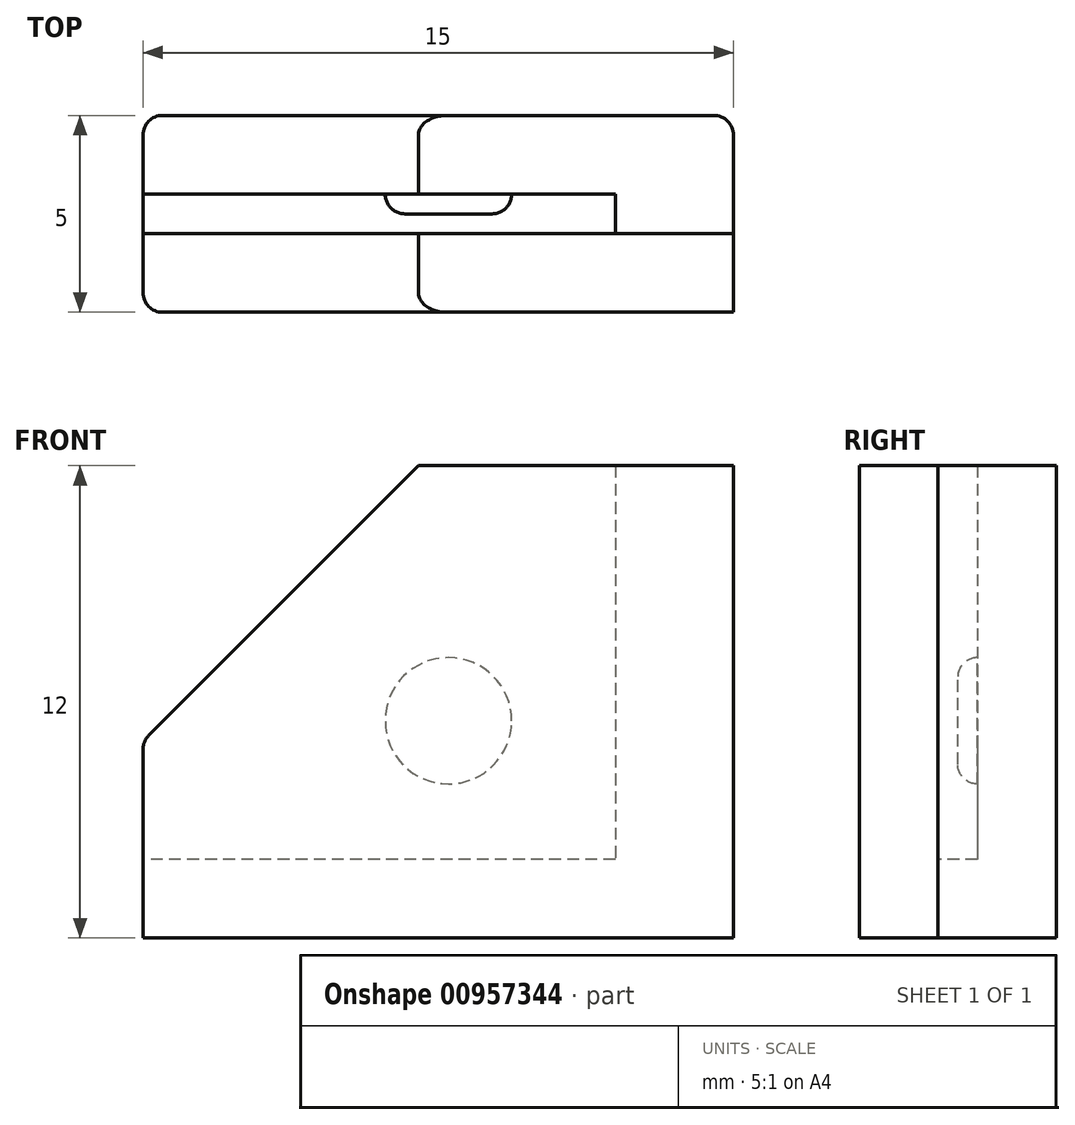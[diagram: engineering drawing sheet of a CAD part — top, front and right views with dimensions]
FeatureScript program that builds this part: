
annotation { "Feature Type Name" : "Feature", "Feature Type Description" : "" }
export const myFeature = defineFeature(function(context is Context, id is Id, definition is map)
    precondition{}
    {
        {
            var Q0;
            Q0=qCreatedBy(makeId("Front.planeOp"),FACE);
            var sketch = newSketch(context, id + "F0", { "sketchPlane" : qUnion([Q0])});
            skLineSegment(sketch, "E0", {"start": v(0, 12) * mm, "end": v(-5, 12) * mm});
            skLineSegment(sketch, "E1", {"start": v(-5, 12) * mm, "end": v(-12, 5) * mm});
            skLineSegment(sketch, "E2", {"start": v(-12, 5) * mm, "end": v(-12, 0) * mm});
            skLineSegment(sketch, "E3", {"start": v(-12, 0) * mm, "end": v(0, 0) * mm});
            skLineSegment(sketch, "E4", {"start": v(0, 12) * mm, "end": v(0, 2) * mm});
            skLineSegment(sketch, "E5", {"start": v(0, 2) * mm, "end": v(-12, 2) * mm});
            skLineSegment(sketch, "E6", {"start": v(0, 12) * mm, "end": v(3, 12) * mm});
            skLineSegment(sketch, "E7", {"start": v(3, 12) * mm, "end": v(3, 0) * mm});
            skLineSegment(sketch, "E8", {"start": v(3, 0) * mm, "end": v(0, 0) * mm});
            skCircle(sketch, "E9", {"center": v(-4.24, 5.52) * mm, "radius": 1.6 * mm});
            skSolve(sketch);
        }
        {
            var Q0;
            {var subQ1=sQuery(id+"F0.wireOp",EDGE,"E1");Q0=makeQuery(id+"F0.imprint","IMPRINT",FACE,{"disambiguationData":[TD([[makeQuery(id+"F0.imprint","IMPRINT",EDGE,{"derivedFrom":subQ1}),1.0]])]});}
            var Q1;
            Q1=makeQuery(id+"F0.imprint","IMPRINT",FACE,{"disambiguationData":[TD([[makeQuery(id+"F0.imprint","IMPRINT",EDGE,{"derivedFrom":sQuery(id+"F0.wireOp",EDGE,"E9")}),1.0]])]});
            var Q2;
            {var subQ1=sQuery(id+"F0.wireOp",EDGE,"E3");Q2=makeQuery(id+"F0.imprint","IMPRINT",FACE,{"disambiguationData":[TD([[makeQuery(id+"F0.imprint","IMPRINT",EDGE,{"derivedFrom":subQ1}),1.0]])]});}
            extrude(context, id + "F1", {"entities" : qUnion([Q0, Q1, Q2]), "oppositeDirection" : true, "depth" : 3 * mm, "offsetDistance" : 25 * mm});
        }
        {
            var Q0;
            {var subQ1=sQuery(id+"F0.wireOp",EDGE,"E1");Q0=makeQuery(id+"F0.imprint","IMPRINT",FACE,{"disambiguationData":[TD([[makeQuery(id+"F0.imprint","IMPRINT",EDGE,{"derivedFrom":subQ1}),1.0]])]});}
            extrude(context, id + "F2", {"entities" : qUnion([Q0]), "operationType" : NewBodyOperationType.REMOVE, "oppositeDirection" : true, "depth" : 1 * mm, "offsetDistance" : 25 * mm});
        }
        {
            var Q0;
            Q0=makeQuery(id+"F0.imprint","IMPRINT",FACE,{"disambiguationData":[TD([[makeQuery(id+"F0.imprint","IMPRINT",EDGE,{"derivedFrom":sQuery(id+"F0.wireOp",EDGE,"E9")}),1.0]])]});
            extrude(context, id + "F3", {"entities" : qUnion([Q0]), "operationType" : NewBodyOperationType.REMOVE, "oppositeDirection" : true, "depth" : 0.5 * mm, "offsetDistance" : 25 * mm});
        }
        {
            var Q0;
            Q0=makeQuery(id+"F3.boolean.opBoolean","COPY",FACE,{"derivedFrom":makeQuery(id+"F3.opExtrude","CAP_FACE",FACE,{"disambiguationData":[OSD([sQuery(id+"F0.wireOp",EDGE,"E9")])],"isStart":false})});
            fillet(context, id + "F4", {"entities" : qUnion([Q0]), "radius" : .5 * mm, "tangentPropagation" : true, "allowEdgeOverflow" : false});
        }
        {
            var Q0;
            {var subQ1=sQuery(id+"F0.wireOp",EDGE,"E1");Q0=makeQuery(id+"F0.imprint","IMPRINT",FACE,{"disambiguationData":[TD([[makeQuery(id+"F0.imprint","IMPRINT",EDGE,{"derivedFrom":subQ1}),1.0]])]});}
            var Q1;
            {var subQ1=sQuery(id+"F0.wireOp",EDGE,"E3");Q1=makeQuery(id+"F0.imprint","IMPRINT",FACE,{"disambiguationData":[TD([[makeQuery(id+"F0.imprint","IMPRINT",EDGE,{"derivedFrom":subQ1}),1.0]])]});}
            var Q2;
            Q2=makeQuery(id+"F0.imprint","IMPRINT",FACE,{"disambiguationData":[TD([[makeQuery(id+"F0.imprint","IMPRINT",EDGE,{"derivedFrom":sQuery(id+"F0.wireOp",EDGE,"E9")}),1.0]])]});
            extrude(context, id + "F5", {"entities" : qUnion([Q0, Q1, Q2]), "depth" : 2 * mm, "offsetDistance" : 25 * mm});
        }
        {
            var Q0;
            Q0=makeQuery(id+"F5.opExtrude","CAP_EDGE",EDGE,{"disambiguationData":[OSD([sQuery(id+"F0.wireOp",EDGE,"E1")])],"isStart":false});
            var Q1;
            Q1=makeQuery(id+"F5.opExtrude","CAP_EDGE",EDGE,{"disambiguationData":[OSD([sQuery(id+"F0.wireOp",EDGE,"E2")])],"isStart":false});
            var Q2;
            Q2=makeQuery(id+"F5.opExtrude","SWEPT_EDGE",EDGE,{"disambiguationData":[OSD([sQuery(id+"F0.wireOp",EDGE,"E1"),sQuery(id+"F0.wireOp",EDGE,"E2")])]});
            fillet(context, id + "F6", {"entities" : qUnion([Q0, Q1, Q2]), "radius" : .5 * mm, "tangentPropagation" : true, "allowEdgeOverflow" : false});
        }
        {
            var Q0;
            Q0=makeQuery(id+"F1.opExtrude","CAP_EDGE",EDGE,{"disambiguationData":[OSD([sQuery(id+"F0.wireOp",EDGE,"E1")])],"isStart":false});
            var Q1;
            Q1=makeQuery(id+"F1.opExtrude","SWEPT_EDGE",EDGE,{"disambiguationData":[OSD([sQuery(id+"F0.wireOp",EDGE,"E1"),sQuery(id+"F0.wireOp",EDGE,"E2")])]});
            var Q2;
            Q2=makeQuery(id+"F1.opExtrude","CAP_EDGE",EDGE,{"disambiguationData":[OSD([sQuery(id+"F0.wireOp",EDGE,"E2")])],"isStart":false});
            var Q3;
            Q3=makeQuery(id+"F1.opExtrude","CAP_EDGE",EDGE,{"disambiguationData":[OSD([sQuery(id+"F0.wireOp",EDGE,"E7")])],"isStart":false});
            fillet(context, id + "F7", {"entities" : qUnion([Q0, Q1, Q2, Q3]), "radius" : .5 * mm, "tangentPropagation" : true, "allowEdgeOverflow" : false});
        }
    });
